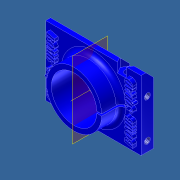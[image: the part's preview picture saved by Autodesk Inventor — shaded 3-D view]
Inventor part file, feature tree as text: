
AUTODESK INVENTOR PART (.ipt)
format: ipt  version: unknown  size: 832,512 bytes
history: native  units: in
note: dims shown in document units (in); Inventor stores cm internally (conversion verified against a paired STEP export)
features: sketch x9, extrude x6, hole x3, fillet x2, projected_geometry x2, other x2, plane x1, pattern_circular x1, chamfer x1
ambient origin geometry x8: Origin, YZ Plane, XZ Plane, XY Plane, X Axis, Y Axis, Z Axis, Center Point
bodies: Solid1 (feature_tree)
feature tree (27):
  extrude  "Extrusion1"  Depth=2.475in
  extrude  "Extrusion2"  Depth=1.1825in
  extrude  "Extrusion3"  Depth=1.2375in
  fillet  "Fillet1"  Radius=0.325in
  extrude  "Extrusion4"  Depth=0.5in TaperAngle=0.0deg
  fillet  "Fillet2"  Radius=0.125in
  hole  "Hole2"  [1 undecoded]
  hole  "Hole3"  [1 undecoded]
  hole  "Hole4"  [1 undecoded]
  extrude  "Extrusion5"  Depth=1.25in
  plane  "Work Plane1"
  pattern_circular  "Circular Pattern1"  [2 undecoded]
  chamfer  "Chamfer1"  Distance=0.25in
  extrude  "Extrusion6"  Depth=1.25in
  sketch  "Sketch1"  dims[d0=1.798in d1=2.475in]
  sketch  "Sketch2"  dims[d2=0.325in d3=0.0in d4=1.1825in]
  sketch  "Sketch3"  dims[d5=0.899in d6=1.2375in d7=0.325in d8=0.0in]
  sketch  "Sketch4"  dims[d9=0.125in d10=0.5in d11=0.0in d12=0.125in]
  sketch  "Sketch6"  dims[d13=0.025in d14=0.025in]
  sketch  "Sketch7"  dims[d15=0.25in d16=0.75in]
  sketch  "Sketch8"  dims[d17=0.325in d18=0.0in d19=0.025in]
  projected_geometry  "Projected Loop3"
  projected_geometry  "Projected Loop4"
  sketch  "Sketch9"  dims[d30=0.25in d31=1.25in]
  other  "Work Axis1"
  other  "Work Axis2"
  sketch  "Sketch10"  dims[d32=0.1625in d33=0.1625in d34=0.156in d35=0.325in d36=0.375in d37=0.25in d38=0.5635in d39=0.5in d40=0.8108in d41=0.25in d42=1.25in d43=0.1625in d44=0.1625in d45=0.156in d46=0.325in d47=0.375in d48=0.25in d49=0.5635in d50=0.5in d51=0.8108in d52=0.1625in d53=0.15in d54=0.177in d55=0.325in d56=0.332in d57=0.25in d58=0.5635in d59=0.5in d60=0.8108in d61=0.1in d62=0.0in d63=0.0in d64=0.7874in d65=360.0deg d67=0.2in d68=0.125in d69=45.0deg d70=0.3625in d71=0.25in d72=0.0in]
note: 5 required parameter values undecoded (feature->parameter linkage not recoverable at this tier; creation-order binding heuristic only, values carry confidence <= 0.55)
